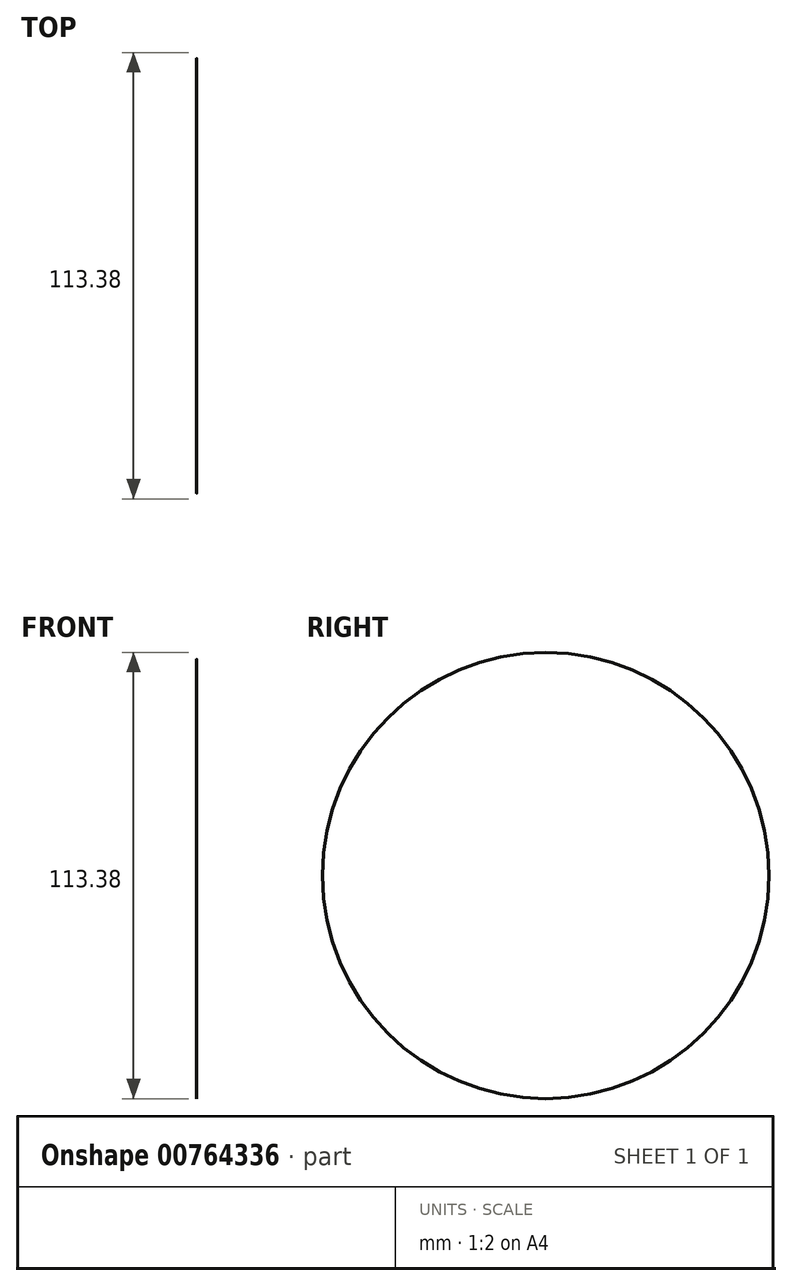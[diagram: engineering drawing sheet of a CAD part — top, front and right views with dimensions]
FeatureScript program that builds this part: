
annotation { "Feature Type Name" : "Feature", "Feature Type Description" : "" }
export const myFeature = defineFeature(function(context is Context, id is Id, definition is map)
    precondition{}
    {
        {
            var Q0;
            Q0=qCreatedBy(makeId("Front.planeOp"),FACE);
            var sketch = newSketch(context, id + "F0", { "sketchPlane" : qUnion([Q0])});
            skLineSegment(sketch, "E0", {"start": v(-29.22, 0) * mm, "end": v(0, 56.69) * mm});
            skPoint(sketch, "E1.end.orphan", {"position": v(29.22, 0) * mm});
            skLineSegment(sketch, "E2", {"start": v(-29.22, 0) * mm, "end": v(0, 0) * mm});
            skLineSegment(sketch, "E3", {"start": v(0, 0) * mm, "end": v(0, 56.69) * mm});
            skSolve(sketch);
        }
        {
            var Q0;
            Q0=sQuery(id+"F0.wireOp",EDGE,"E3");
            var Q1;
            Q1=sQuery(id+"F0.wireOp",EDGE,"E2");
            revolve(context, id + "F1", {"bodyType" : ToolBodyType.SURFACE, "surfaceOperationType" : NewSurfaceOperationType.NEW, "surfaceEntities" : qUnion([Q0]), "axis" : qUnion([Q1]), "revolveType" : RevolveType.FULL});
        }
    });
